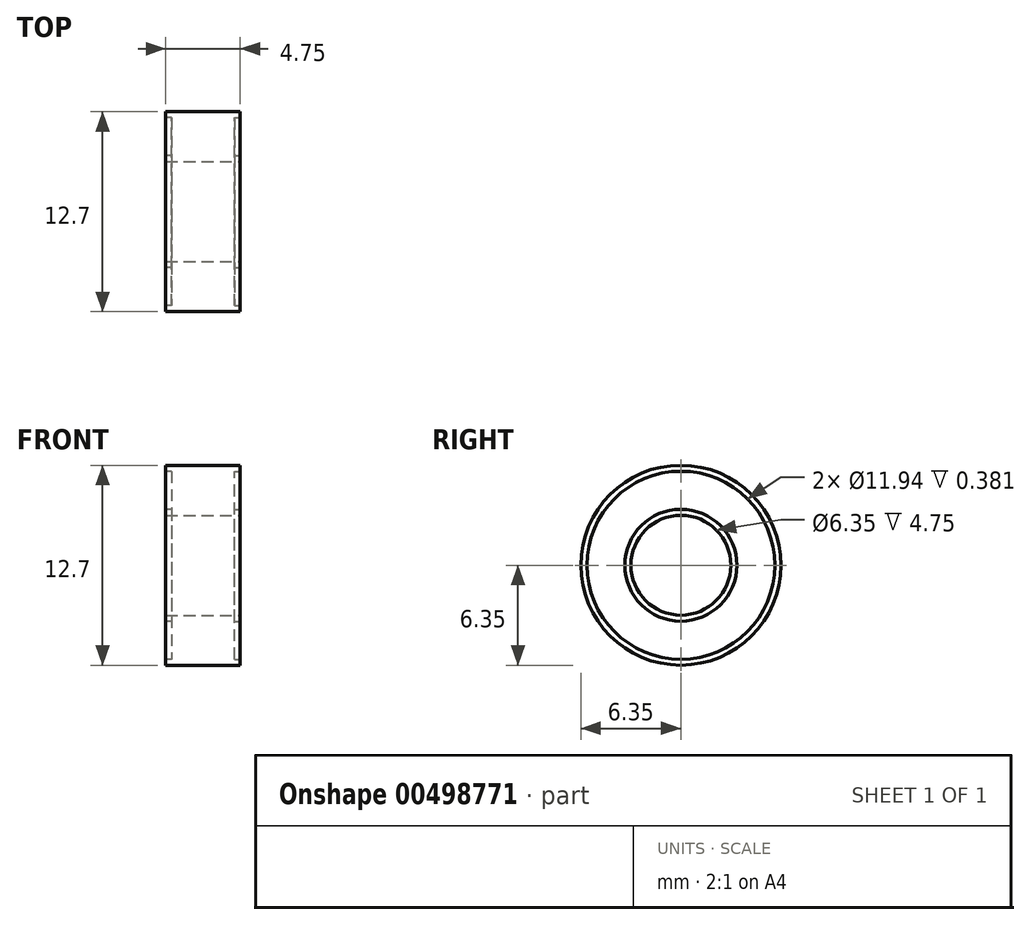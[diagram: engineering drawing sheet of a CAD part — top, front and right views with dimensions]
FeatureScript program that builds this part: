
annotation { "Feature Type Name" : "Feature", "Feature Type Description" : "" }
export const myFeature = defineFeature(function(context is Context, id is Id, definition is map)
    precondition{}
    {
        {
            var Q0;
            Q0=qCreatedBy(makeId("Right.planeOp"),FACE);
            var sketch = newSketch(context, id + "F0", { "sketchPlane" : qUnion([Q0])});
            skCircle(sketch, "E0", {"center": v(0, 0) * mm, "radius": 6.35 * mm});
            skSolve(sketch);
        }
        {
            var Q0;
            Q0=makeQuery(id+"F0.imprint","IMPRINT",FACE,{"disambiguationData":[TD([[makeQuery(id+"F0.imprint","IMPRINT",EDGE,{"derivedFrom":sQuery(id+"F0.wireOp",EDGE,"E0")}),1.0]])]});
            extrude(context, id + "F1", {"entities" : qUnion([Q0]), "depth" : 4.75 * mm});
        }
        {
            var Q0;
            Q0=makeQuery(id+"F1.opExtrude","CAP_FACE",FACE,{"disambiguationData":[OSD([sQuery(id+"F0.wireOp",EDGE,"E0")])],"isStart":false});
            var sketch = newSketch(context, id + "F2", { "sketchPlane" : qUnion([Q0])});
            skCircle(sketch, "E1", {"center": v(0, 0) * mm, "radius": 3.18 * mm});
            skSolve(sketch);
        }
        {
            var Q0;
            Q0=makeQuery(id+"F2.imprint","IMPRINT",FACE,{"disambiguationData":[TD([[makeQuery(id+"F2.imprint","IMPRINT",EDGE,{"derivedFrom":sQuery(id+"F2.wireOp",EDGE,"E1")}),1.0]])]});
            extrude(context, id + "F3", {"entities" : qUnion([Q0]), "operationType" : NewBodyOperationType.REMOVE, "oppositeDirection" : true, "depth" : 25.4 * mm});
        }
        {
            var Q0;
            Q0=makeQuery(id+"F1.opExtrude","CAP_FACE",FACE,{"disambiguationData":[OSD([sQuery(id+"F0.wireOp",EDGE,"E0")])],"isStart":false});
            var sketch = newSketch(context, id + "F4", { "sketchPlane" : qUnion([Q0])});
            skLineSegment(sketch, "E2", {"start": v(0, 3.18) * mm, "end": v(0, 3.56) * mm});
            skLineSegment(sketch, "E3", {"start": v(0, 6.35) * mm, "end": v(0, 5.97) * mm});
            skLineSegment(sketch, "E4", {"start": v(0, -3.18) * mm, "end": v(0, -3.56) * mm});
            skLineSegment(sketch, "E5", {"start": v(0, -6.35) * mm, "end": v(0, -5.97) * mm});
            skCircle(sketch, "E6", {"center": v(0, 0) * mm, "radius": 3.56 * mm});
            skCircle(sketch, "E7", {"center": v(0, 0) * mm, "radius": 5.97 * mm});
            skSolve(sketch);
        }
        {
            var Q0;
            {var subQ0=sQuery(id+"F4.wireOp",EDGE,"E6");var subQ1=makeQuery(id+"F4.imprint","INTERSECT",VERTEX,{"derivedFrom":[sQuery(id+"F4.wireOp",EDGE,"E2"),subQ0]});Q0=makeQuery(id+"F4.imprint","IMPRINT",FACE,{"disambiguationData":[TD([[makeQuery(id+"F4.imprint","IMPRINT",EDGE,{"disambiguationData":[TD([[subQ1,-1.0]])],"derivedFrom":subQ0}),-1.0]])]});}
            extrude(context, id + "F5", {"entities" : qUnion([Q0]), "operationType" : NewBodyOperationType.REMOVE, "oppositeDirection" : true, "depth" : 0.38 * mm});
        }
        {
            var Q0;
            Q0=makeQuery(id+"F1.opExtrude","CAP_FACE",FACE,{"disambiguationData":[OSD([sQuery(id+"F0.wireOp",EDGE,"E0")])],"isStart":true});
            var sketch = newSketch(context, id + "F6", { "sketchPlane" : qUnion([Q0])});
            skLineSegment(sketch, "E8", {"start": v(0, 3.18) * mm, "end": v(0, 3.56) * mm});
            skLineSegment(sketch, "E9", {"start": v(0, 6.35) * mm, "end": v(0, 5.97) * mm});
            skLineSegment(sketch, "E10", {"start": v(0, -3.18) * mm, "end": v(0, -3.56) * mm});
            skLineSegment(sketch, "E11", {"start": v(0, -6.35) * mm, "end": v(0, -5.97) * mm});
            skCircle(sketch, "E12", {"center": v(0, 0) * mm, "radius": 3.56 * mm});
            skCircle(sketch, "E13", {"center": v(0, 0) * mm, "radius": 5.97 * mm});
            skSolve(sketch);
        }
        {
            var Q0;
            {var subQ0=sQuery(id+"F6.wireOp",EDGE,"E12");var subQ1=makeQuery(id+"F6.imprint","INTERSECT",VERTEX,{"derivedFrom":[sQuery(id+"F6.wireOp",EDGE,"E8"),subQ0]});Q0=makeQuery(id+"F6.imprint","IMPRINT",FACE,{"disambiguationData":[TD([[makeQuery(id+"F6.imprint","IMPRINT",EDGE,{"disambiguationData":[TD([[subQ1,-1.0]])],"derivedFrom":subQ0}),-1.0]])]});}
            extrude(context, id + "F7", {"entities" : qUnion([Q0]), "operationType" : NewBodyOperationType.REMOVE, "oppositeDirection" : true, "depth" : 0.38 * mm});
        }
    });
